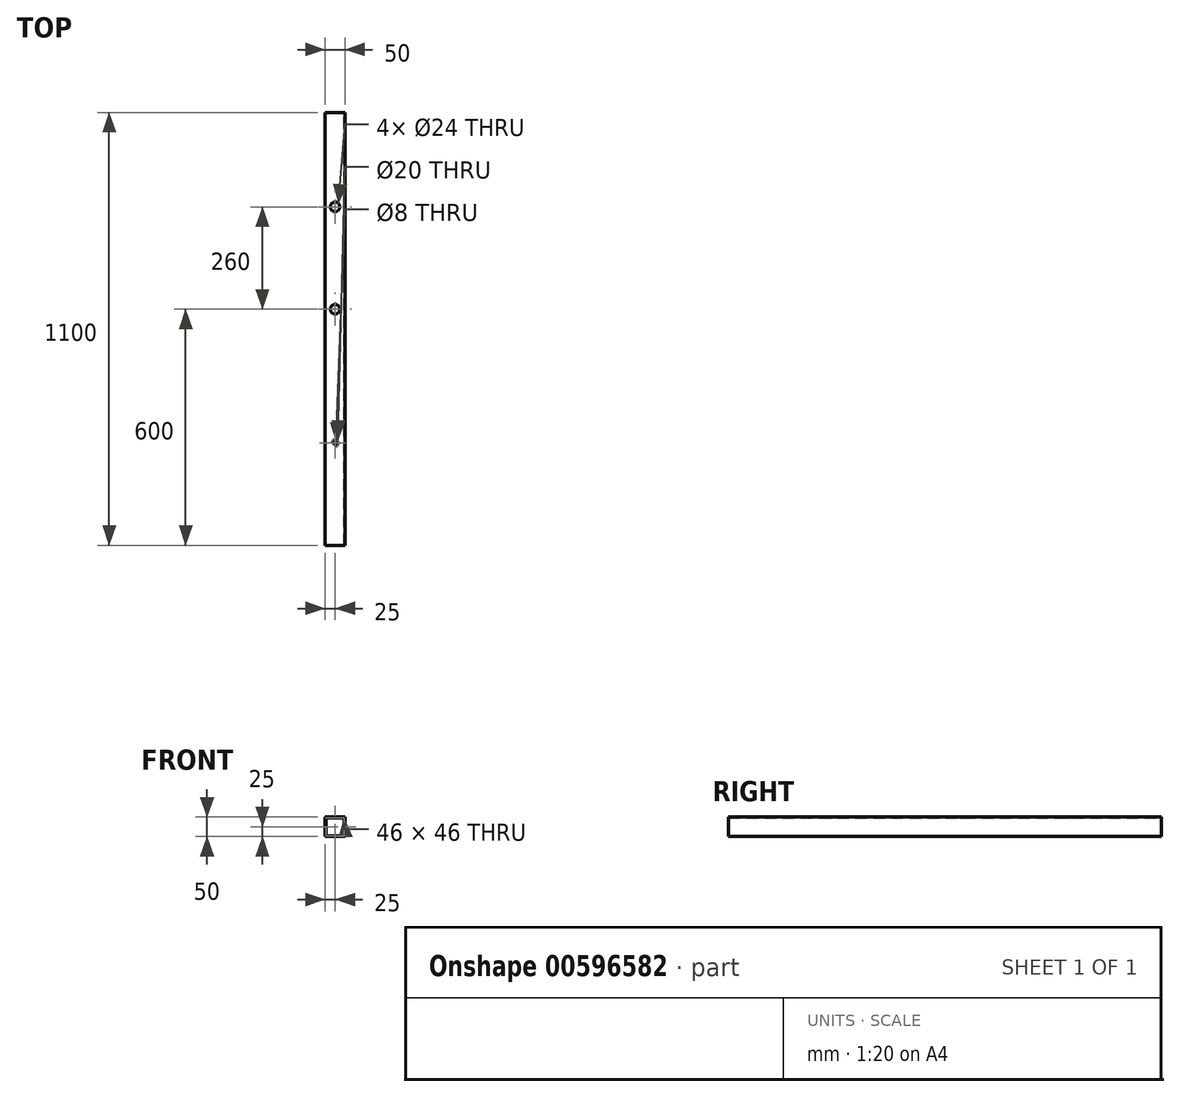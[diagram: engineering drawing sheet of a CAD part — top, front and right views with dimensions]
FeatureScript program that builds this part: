
annotation { "Feature Type Name" : "Feature", "Feature Type Description" : "" }
export const myFeature = defineFeature(function(context is Context, id is Id, definition is map)
    precondition{}
    {
        {
            var Q0;
            Q0=qCreatedBy(makeId("Front.planeOp"),FACE);
            var sketch = newSketch(context, id + "F0", { "sketchPlane" : qUnion([Q0])});
            skLineSegment(sketch, "E0.bottom", {"start": v(0, 0) * mm, "end": v(50, 0) * mm});
            skLineSegment(sketch, "E0.top", {"start": v(0, 50) * mm, "end": v(50, 50) * mm});
            skLineSegment(sketch, "E0.left", {"start": v(0, 0) * mm, "end": v(0, 50) * mm});
            skLineSegment(sketch, "E0.right", {"start": v(50, 0) * mm, "end": v(50, 50) * mm});
            skLineSegment(sketch, "E1.bottom", {"start": v(2, 48) * mm, "end": v(48, 48) * mm});
            skLineSegment(sketch, "E1.top", {"start": v(2, 2) * mm, "end": v(48, 2) * mm});
            skLineSegment(sketch, "E1.left", {"start": v(2, 48) * mm, "end": v(2, 2) * mm});
            skLineSegment(sketch, "E1.right", {"start": v(48, 48) * mm, "end": v(48, 2) * mm});
            skSolve(sketch);
        }
        {
            var Q0;
            Q0=makeQuery(id+"F0.imprint","IMPRINT",FACE,{"disambiguationData":[TD([[makeQuery(id+"F0.imprint","IMPRINT",EDGE,{"derivedFrom":sQuery(id+"F0.wireOp",EDGE,"E0.bottom")}),1.0]])]});
            extrude(context, id + "F1", {"entities" : qUnion([Q0]), "depth" : 1100 * mm, "offsetDistance" : 25 * mm});
        }
        {
            var Q0;
            Q0=makeQuery(id+"F1.opExtrude","SWEPT_FACE",FACE,{"disambiguationData":[OSD([sQuery(id+"F0.wireOp",EDGE,"E0.top")])]});
            var sketch = newSketch(context, id + "F2", { "sketchPlane" : qUnion([Q0])});
            skCircle(sketch, "E2", {"center": v(25, -240) * mm, "radius": 12 * mm});
            skPoint(sketch, "E2.centerSnap0", {"position": v(25, 0) * mm});
            skCircle(sketch, "E3", {"center": v(25, -500) * mm, "radius": 12 * mm});
            skSolve(sketch);
        }
        {
            var Q0;
            Q0=makeQuery(id+"F2.imprint","IMPRINT",FACE,{"disambiguationData":[TD([[makeQuery(id+"F2.imprint","IMPRINT",EDGE,{"derivedFrom":sQuery(id+"F2.wireOp",EDGE,"E3")}),1.0]])]});
            var Q1;
            Q1=makeQuery(id+"F2.imprint","IMPRINT",FACE,{"disambiguationData":[TD([[makeQuery(id+"F2.imprint","IMPRINT",EDGE,{"derivedFrom":sQuery(id+"F2.wireOp",EDGE,"E2")}),1.0]])]});
            extrude(context, id + "F3", {"entities" : qUnion([Q0, Q1]), "operationType" : NewBodyOperationType.REMOVE, "endBound" : BoundingType.THROUGH_ALL, "oppositeDirection" : true, "depth" : 25 * mm, "offsetDistance" : 25 * mm});
        }
        {
            var Q0;
            Q0=makeQuery(id+"F1.opExtrude","SWEPT_FACE",FACE,{"disambiguationData":[OSD([sQuery(id+"F0.wireOp",EDGE,"E0.top")])]});
            var sketch = newSketch(context, id + "F4", { "sketchPlane" : qUnion([Q0])});
            skCircle(sketch, "E4", {"center": v(25, -840) * mm, "radius": 10 * mm});
            skSolve(sketch);
        }
        {
            var Q0;
            Q0 = qSketchRegion(id + "F4", true);
            extrude(context, id + "F5", {"entities" : qUnion([Q0]), "operationType" : NewBodyOperationType.REMOVE, "endBound" : BoundingType.THROUGH_ALL, "oppositeDirection" : true, "depth" : 25 * mm, "offsetDistance" : 25 * mm});
        }
        {
            var Q0;
            Q0=makeQuery(id+"F1.opExtrude","SWEPT_FACE",FACE,{"disambiguationData":[OSD([sQuery(id+"F0.wireOp",EDGE,"E0.top")])]});
            var sketch = newSketch(context, id + "F6", { "sketchPlane" : qUnion([Q0])});
            skCircle(sketch, "E5", {"center": v(25, -840) * mm, "radius": 10 * mm});
            skCircle(sketch, "E6", {"center": v(25, -840) * mm, "radius": 4 * mm});
            skSolve(sketch);
        }
        {
            var Q0;
            Q0=makeQuery(id+"F6.imprint","IMPRINT",FACE,{"disambiguationData":[TD([[makeQuery(id+"F6.imprint","IMPRINT",EDGE,{"derivedFrom":sQuery(id+"F6.wireOp",EDGE,"E5")}),1.0]])]});
            extrude(context, id + "F7", {"entities" : qUnion([Q0]), "operationType" : NewBodyOperationType.ADD, "oppositeDirection" : true, "depth" : 2 * mm, "offsetDistance" : 25 * mm});
        }
    });
